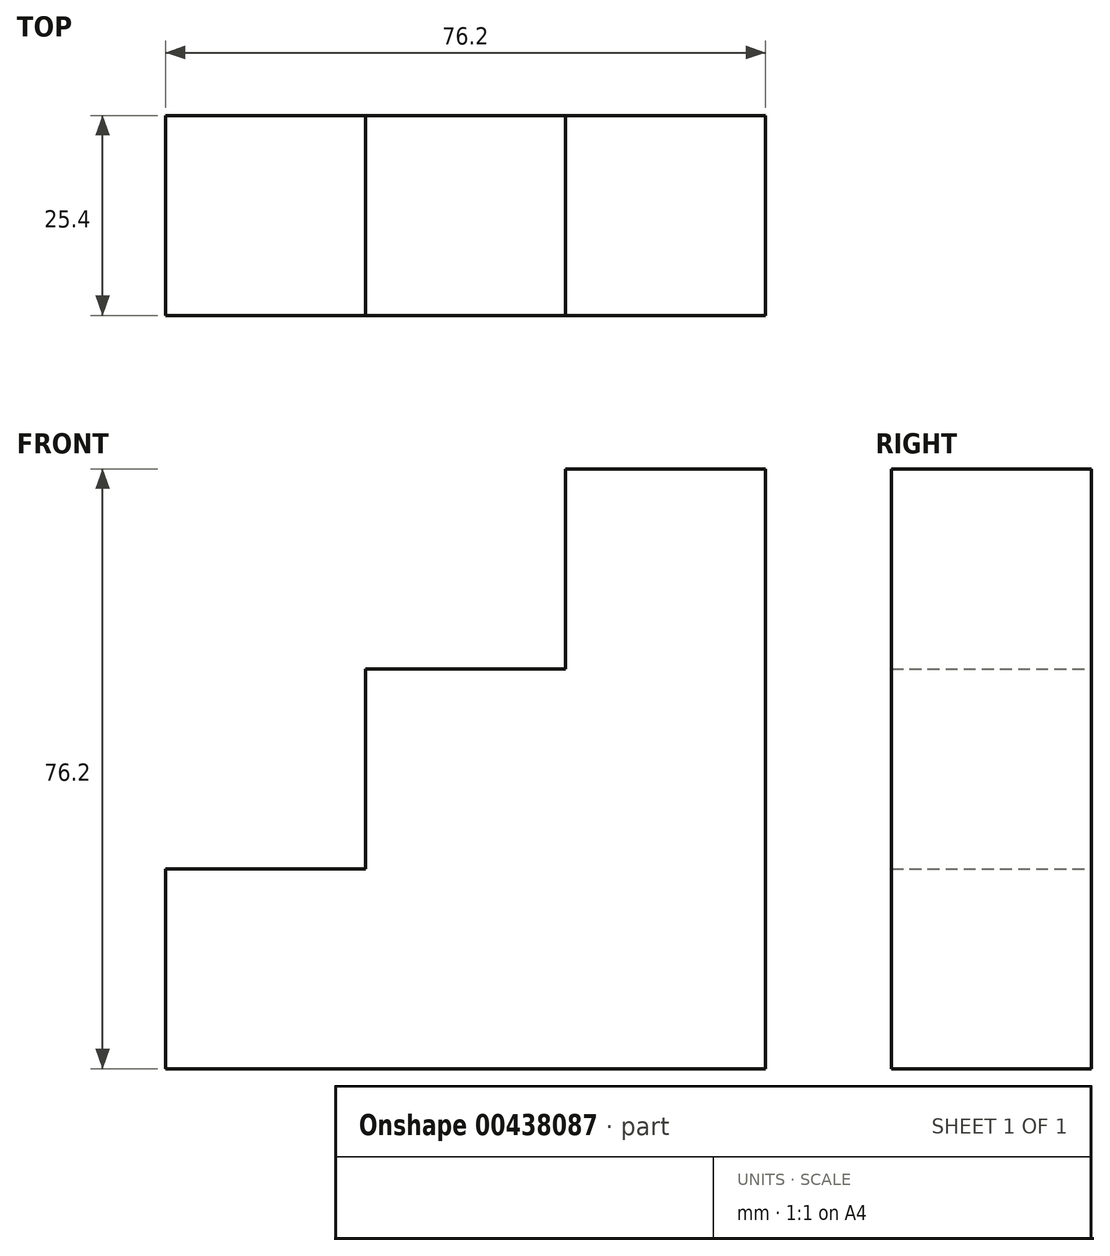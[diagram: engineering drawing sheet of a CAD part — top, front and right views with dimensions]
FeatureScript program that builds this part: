
annotation { "Feature Type Name" : "Feature", "Feature Type Description" : "" }
export const myFeature = defineFeature(function(context is Context, id is Id, definition is map)
    precondition{}
    {
        {
            var Q0;
            Q0=qCreatedBy(makeId("Front.planeOp"),FACE);
            var sketch = newSketch(context, id + "F0", { "sketchPlane" : qUnion([Q0])});
            skLineSegment(sketch, "E0", {"start": v(40.46, 29.8) * mm, "end": v(15.06, 29.8) * mm});
            skLineSegment(sketch, "E1", {"start": v(15.06, 29.8) * mm, "end": v(15.06, 4.4) * mm});
            skLineSegment(sketch, "E2", {"start": v(15.06, 4.4) * mm, "end": v(-10.34, 4.4) * mm});
            skLineSegment(sketch, "E3", {"start": v(-10.34, 4.4) * mm, "end": v(-10.34, -21) * mm});
            skLineSegment(sketch, "E4", {"start": v(-10.34, -21) * mm, "end": v(-35.74, -21) * mm});
            skLineSegment(sketch, "E5", {"start": v(-35.74, -21) * mm, "end": v(-35.74, -46.4) * mm});
            skLineSegment(sketch, "E6", {"start": v(-35.74, -46.4) * mm, "end": v(40.46, -46.4) * mm});
            skLineSegment(sketch, "E7", {"start": v(40.46, -46.4) * mm, "end": v(40.46, 29.8) * mm});
            skSolve(sketch);
        }
        {
            var Q0;
            Q0=makeQuery(id+"F0.imprint","IMPRINT",FACE,{"disambiguationData":[TD([[makeQuery(id+"F0.imprint","IMPRINT",EDGE,{"derivedFrom":sQuery(id+"F0.wireOp",EDGE,"E0")}),1.0]])]});
            extrude(context, id + "F1", {"entities" : qUnion([Q0]), "depth" : 25.4 * mm});
        }
    });
